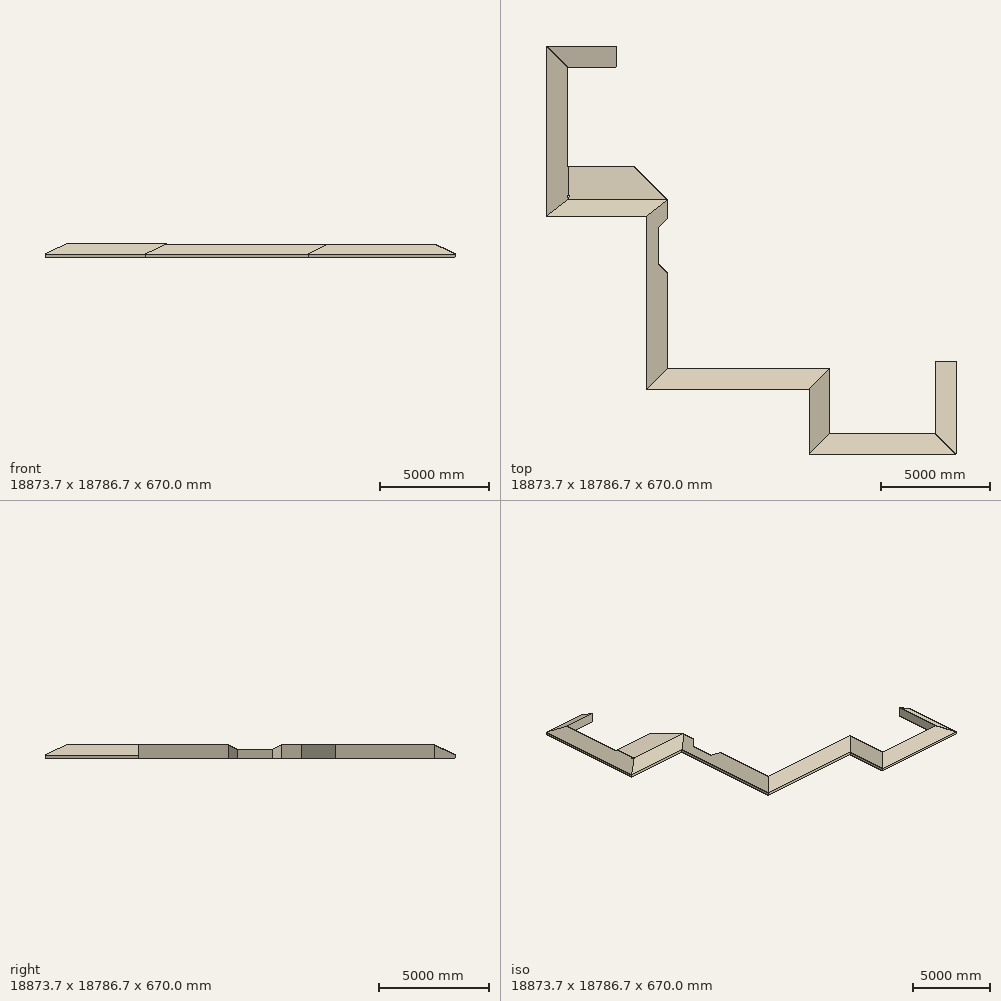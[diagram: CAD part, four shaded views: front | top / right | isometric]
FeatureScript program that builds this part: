
annotation { "Feature Type Name" : "Feature", "Feature Type Description" : "" }
export const myFeature = defineFeature(function(context is Context, id is Id, definition is map)
    precondition{}
    {
        {
            var Q0;
            Q0=qCreatedBy(makeId("Top.planeOp"),FACE);
            var sketch = newSketch(context, id + "F0", { "sketchPlane" : qUnion([Q0])});
            skLineSegment(sketch, "E0", {"start": v(-70, 0) * mm, "end": v(-4950, 0) * mm});
            skLineSegment(sketch, "E1", {"start": v(-5020, 70) * mm, "end": v(-5020, 3000) * mm});
            skLineSegment(sketch, "E2", {"start": v(-5020, 3000) * mm, "end": v(-12430, 3000) * mm});
            skLineSegment(sketch, "E3", {"start": v(-12500, 3070) * mm, "end": v(-12500, 7455) * mm});
            skLineSegment(sketch, "E4", {"start": v(-12500, 7455) * mm, "end": v(-12924.26, 7879.26) * mm});
            skLineSegment(sketch, "E5", {"start": v(-12924.26, 7879.26) * mm, "end": v(-12924.26, 9559.26) * mm});
            skLineSegment(sketch, "E6", {"start": v(-12924.26, 9559.26) * mm, "end": v(-12500, 9983.53) * mm});
            skLineSegment(sketch, "E7", {"start": v(-12500, 9983.53) * mm, "end": v(-12500, 10813.53) * mm});
            skLineSegment(sketch, "E8", {"start": v(-12500, 10813.53) * mm, "end": v(-14013.2, 12326.74) * mm});
            skLineSegment(sketch, "E9", {"start": v(-14013.2, 12326.74) * mm, "end": v(-17043.7, 12326.74) * mm});
            skLineSegment(sketch, "E10", {"start": v(-17113.7, 12396.74) * mm, "end": v(-17113.7, 16956.74) * mm});
            skLineSegment(sketch, "E11.0", {"start": v(-17043.7, 12396.74) * mm, "end": v(-17043.7, 16956.74) * mm});
            skLineSegment(sketch, "E12.0", {"start": v(-12430, 10842.52) * mm, "end": v(-13984.21, 12396.74) * mm});
            skLineSegment(sketch, "E13.0", {"start": v(-12430, 9954.53) * mm, "end": v(-12430, 10842.52) * mm});
            skLineSegment(sketch, "E13.1", {"start": v(-12854.26, 9530.27) * mm, "end": v(-12430, 9954.53) * mm});
            skLineSegment(sketch, "E14.0", {"start": v(-12854.26, 7908.26) * mm, "end": v(-12854.26, 9530.27) * mm});
            skLineSegment(sketch, "E15.0", {"start": v(-12430, 7484) * mm, "end": v(-12854.26, 7908.26) * mm});
            skLineSegment(sketch, "E16.0", {"start": v(-12430, 3070) * mm, "end": v(-12430, 7484) * mm});
            skLineSegment(sketch, "E17.0", {"start": v(-4950, 3070) * mm, "end": v(-12430, 3070) * mm});
            skLineSegment(sketch, "E18.0", {"start": v(-4950, 70) * mm, "end": v(-4950, 3070) * mm});
            skLineSegment(sketch, "E19.0", {"start": v(-70, 70) * mm, "end": v(-4950, 70) * mm});
            skLineSegment(sketch, "E20.0", {"start": v(-70, 3398.34) * mm, "end": v(-70, 70) * mm});
            skLineSegment(sketch, "E21", {"start": v(-13984.21, 12396.74) * mm, "end": v(-17043.7, 12396.74) * mm});
            skLineSegment(sketch, "E22", {"start": v(-17113.7, 12326.74) * mm, "end": v(-17113.7, 12176.74) * mm});
            skLineSegment(sketch, "E23", {"start": v(-17113.7, 12176.74) * mm, "end": v(-17043.7, 12176.74) * mm});
            skLineSegment(sketch, "E24", {"start": v(-17043.7, 12176.74) * mm, "end": v(-17043.7, 12326.74) * mm});
            skLineSegment(sketch, "E25", {"start": v(-17113.7, 12326.74) * mm, "end": v(-17263.7, 12326.74) * mm});
            skLineSegment(sketch, "E26", {"start": v(-17263.7, 12326.74) * mm, "end": v(-17263.7, 12396.74) * mm});
            skLineSegment(sketch, "E27", {"start": v(-17263.7, 12396.74) * mm, "end": v(-17113.7, 12396.74) * mm});
            skLineSegment(sketch, "E28", {"start": v(-12500, 3000) * mm, "end": v(-12650, 3000) * mm});
            skLineSegment(sketch, "E29", {"start": v(-12650, 3000) * mm, "end": v(-12650, 3070) * mm});
            skLineSegment(sketch, "E30", {"start": v(-12650, 3070) * mm, "end": v(-12500, 3070) * mm});
            skLineSegment(sketch, "E31", {"start": v(-12500, 3000) * mm, "end": v(-12500, 2850) * mm});
            skLineSegment(sketch, "E32", {"start": v(-12500, 2850) * mm, "end": v(-12430, 2850) * mm});
            skLineSegment(sketch, "E33", {"start": v(-12430, 2850) * mm, "end": v(-12430, 3000) * mm});
            skLineSegment(sketch, "E34", {"start": v(-5020, 0) * mm, "end": v(-5170, 0) * mm});
            skLineSegment(sketch, "E35", {"start": v(-5170, 0) * mm, "end": v(-5170, 70) * mm});
            skLineSegment(sketch, "E36", {"start": v(-5170, 70) * mm, "end": v(-5020, 70) * mm});
            skLineSegment(sketch, "E37.0", {"start": v(880, 3398.34) * mm, "end": v(880, -880) * mm});
            skLineSegment(sketch, "E38.0", {"start": v(880, -880) * mm, "end": v(-5900, -880) * mm});
            skLineSegment(sketch, "E39.0", {"start": v(-5900, -880) * mm, "end": v(-5900, 2120) * mm});
            skLineSegment(sketch, "E40.0", {"start": v(-5900, 2120) * mm, "end": v(-13380, 2120) * mm});
            skLineSegment(sketch, "E41.0", {"start": v(-13380, 2120) * mm, "end": v(-13380, 10080.66) * mm});
            skLineSegment(sketch, "E42.0", {"start": v(-17993.7, 10080.66) * mm, "end": v(-17993.7, 17906.74) * mm});
            skPoint(sketch, "E43.start.orphan", {"position": v(0, 0) * mm});
            skLineSegment(sketch, "E44", {"start": v(-70, 3398.34) * mm, "end": v(880, 3398.34) * mm});
            skLineSegment(sketch, "E45", {"start": v(-17043.7, 11066.74) * mm, "end": v(-17043.7, 10946.74) * mm});
            skLineSegment(sketch, "E46", {"start": v(-17043.7, 10946.74) * mm, "end": v(-16923.7, 10946.74) * mm});
            skLineSegment(sketch, "E47", {"start": v(-16923.7, 10946.74) * mm, "end": v(-16923.7, 11066.74) * mm});
            skLineSegment(sketch, "E48", {"start": v(-16923.7, 11066.74) * mm, "end": v(-17043.7, 11066.74) * mm});
            skLineSegment(sketch, "E49", {"start": v(-17993.7, 10080.66) * mm, "end": v(-13380, 10080.66) * mm});
            skLineSegment(sketch, "E50", {"start": v(-17263.7, 17026.74) * mm, "end": v(-17113.7, 17026.74) * mm});
            skLineSegment(sketch, "E51.0", {"start": v(-17263.7, 16956.74) * mm, "end": v(-17113.7, 16956.74) * mm});
            skLineSegment(sketch, "E52.0", {"start": v(-17993.7, 17906.74) * mm, "end": v(-14568.05, 17906.74) * mm});
            skLineSegment(sketch, "E53", {"start": v(-14749.94, 18084.32) * mm, "end": v(-14749.94, 16559) * mm});
            skLineSegment(sketch, "E54", {"start": v(-17263.7, 17026.74) * mm, "end": v(-17263.7, 16956.74) * mm});
            skLineSegment(sketch, "E55", {"start": v(-17113.7, 17176.74) * mm, "end": v(-17043.7, 17176.74) * mm});
            skLineSegment(sketch, "E56.trimOffspring", {"start": v(-17043.7, 17026.74) * mm, "end": v(-17043.7, 17176.74) * mm});
            skLineSegment(sketch, "E57.trimOffspring", {"start": v(-17043.7, 16956.74) * mm, "end": v(-14568.05, 16956.74) * mm});
            skLineSegment(sketch, "E58.trimOffspring", {"start": v(-17043.7, 17026.74) * mm, "end": v(-14568.05, 17026.74) * mm});
            skLineSegment(sketch, "E59.trimOffspring", {"start": v(-17113.7, 17026.74) * mm, "end": v(-17113.7, 17176.74) * mm});
            skSolve(sketch);
        }
        {
            var Q0;
            {var subQ0=sQuery(id+"F0.wireOp",EDGE,"E9");Q0=makeQuery(id+"F0.imprint","IMPRINT",FACE,{"disambiguationData":[TD([[makeQuery(id+"F0.imprint","IMPRINT",EDGE,{"derivedFrom":subQ0}),-1.0]])]});}
            var Q1;
            Q1=makeQuery(id+"F0.imprint","IMPRINT",FACE,{"disambiguationData":[TD([[makeQuery(id+"F0.imprint","IMPRINT",EDGE,{"derivedFrom":sQuery(id+"F0.wireOp",EDGE,"E11.0")}),1.0]])]});
            extrude(context, id + "F1", {"entities" : qUnion([Q0, Q1]), "depth" : 670 * mm, "offsetDistance" : 25 * mm});
        }
        {
            var Q0;
            Q0=makeQuery(id+"F1.opExtrude","CAP_EDGE",EDGE,{"disambiguationData":[OSD([sQuery(id+"F0.wireOp",EDGE,"E39.0")])],"isStart":false});
            var Q1;
            Q1=makeQuery(id+"F1.opExtrude","CAP_EDGE",EDGE,{"disambiguationData":[OSD([sQuery(id+"F0.wireOp",EDGE,"E37.0")])],"isStart":false});
            var Q2;
            Q2=makeQuery(id+"F1.opExtrude","CAP_EDGE",EDGE,{"disambiguationData":[OSD([sQuery(id+"F0.wireOp",EDGE,"E41.0")])],"isStart":false});
            var Q3;
            Q3=makeQuery(id+"F1.opExtrude","CAP_EDGE",EDGE,{"disambiguationData":[OSD([sQuery(id+"F0.wireOp",EDGE,"E42.0")])],"isStart":false});
            chamfer(context, id + "F2", {"entities" : qUnion([Q0, Q1, Q2, Q3]), "chamferType" : ChamferType.OFFSET_ANGLE, "width" : 500 * mm, "oppositeDirection" : false, "angle" : 64 * degree, "tangentPropagation" : true});
        }
        {
            var Q0;
            Q0=makeQuery(id+"F1.opExtrude","CAP_EDGE",EDGE,{"disambiguationData":[OSD([sQuery(id+"F0.wireOp",EDGE,"E40.0")])],"isStart":false});
            var Q1;
            Q1=makeQuery(id+"F1.opExtrude","CAP_EDGE",EDGE,{"disambiguationData":[OSD([sQuery(id+"F0.wireOp",EDGE,"E38.0")])],"isStart":false});
            var Q2;
            Q2=makeQuery(id+"F1.opExtrude","CAP_EDGE",EDGE,{"disambiguationData":[OSD([sQuery(id+"F0.wireOp",EDGE,"E52.0")])],"isStart":false});
            chamfer(context, id + "F3", {"entities" : qUnion([Q0, Q1, Q2]), "chamferType" : ChamferType.OFFSET_ANGLE, "width" : 500 * mm, "oppositeDirection" : false, "angle" : 64 * degree, "tangentPropagation" : true});
        }
        {
            var Q0;
            Q0=makeQuery(id+"F1.opExtrude","CAP_EDGE",EDGE,{"disambiguationData":[OSD([sQuery(id+"F0.wireOp",EDGE,"E49")])],"isStart":false});
            chamfer(context, id + "F4", {"entities" : qUnion([Q0]), "chamferType" : ChamferType.TWO_OFFSETS, "width1" : 800 * mm, "oppositeDirection" : false, "width2" : 500 * mm, "tangentPropagation" : true});
        }
    });
